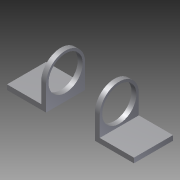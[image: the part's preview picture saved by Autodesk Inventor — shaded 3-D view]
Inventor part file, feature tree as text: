
AUTODESK INVENTOR PART (.ipt)
format: ipt  version: 2012 (Build 160160000, 160)  size: 113,152 bytes
history: native  units: in
note: dims shown in document units (in); Inventor stores cm internally (conversion verified against a paired STEP export)
features: extrude x2, sketch x2
ambient origin geometry x8: Origin, YZ Plane, XZ Plane, XY Plane, X Axis, Y Axis, Z Axis, Center Point
bodies: Solid1 (feature_tree)
feature tree (4):
  extrude  "Extrusion1"  Depth=0.125in
  extrude  "Extrusion2"  Depth=1.125in
  sketch  "Sketch1"  dims[d0=0.125in d1=0.125in]
  sketch  "Sketch2"  dims[d2=1.0in d3=1.125in d4=0.625in d5=1.0in d6=0.0in d7=0.875in d8=0.625in d9=0.5in d10=1.0in d11=0.0in]
